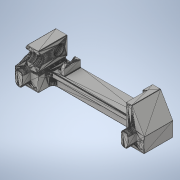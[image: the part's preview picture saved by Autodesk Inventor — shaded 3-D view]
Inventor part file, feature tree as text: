
AUTODESK INVENTOR PART (.ipt)
format: ipt  version: 2021.2 (Build 252289000, 289)  size: 8,477,696 bytes
history: mixed  units: in
note: dims shown in document units (in); Inventor stores cm internally (conversion verified against a paired STEP export)
features: hole x2, sketch x2, imported_body x1
ambient origin geometry x8: Origin, YZ Plane, XZ Plane, XY Plane, X Axis, Y Axis, Z Axis, Center Point
bodies: Solid1 (imported_parasolid), Body1 (imported_parasolid)
feature tree (5):
  hole  "Hole3"  [1 undecoded]
  hole  "Hole4"  [1 undecoded]
  sketch  "Sketch2"  dims[d2=3.937in]
  sketch  "Sketch3"  dims[d17=3.12in d18=0.2362in d19=3.16in d20=2.92in d21=90.0deg d22=0.83in d23=0.0in d24=3.937in d26=3.12in d27=0.2362in d28=3.16in d29=2.92in d30=90.0deg d31=0.83in d32=0.0in d33=3.937in d34=3.937in]
  imported_body  NMx_Import_Brep_tag  [imported B-rep: ~16493 faces, bbox_mm=[1580.222149, 440.000019, 448.500013]]
note: 2 required parameter values undecoded (feature->parameter linkage not recoverable at this tier; creation-order binding heuristic only, values carry confidence <= 0.55)
